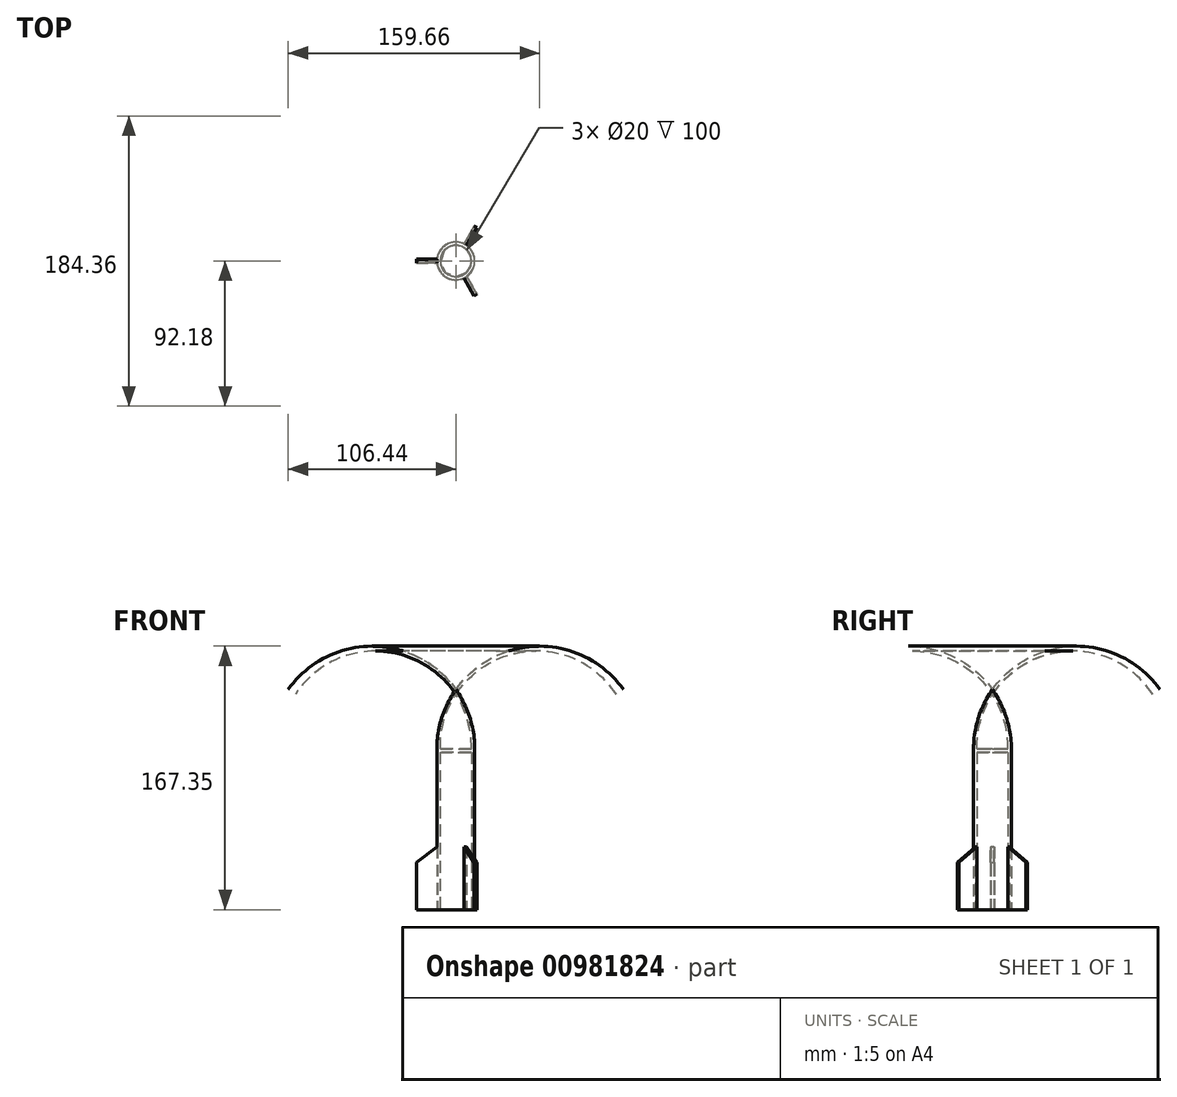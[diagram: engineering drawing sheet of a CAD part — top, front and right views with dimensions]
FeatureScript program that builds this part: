
annotation { "Feature Type Name" : "Feature", "Feature Type Description" : "" }
export const myFeature = defineFeature(function(context is Context, id is Id, definition is map)
    precondition{}
    {
        {
            var Q0;
            Q0=qCreatedBy(makeId("Front.planeOp"),FACE);
            var sketch = newSketch(context, id + "F0", { "sketchPlane" : qUnion([Q0])});
            skLineSegment(sketch, "E0", {"start": v(0, 0) * mm, "end": v(0, 102) * mm});
            skLineSegment(sketch, "E1", {"start": v(-12, 102.13) * mm, "end": v(-12, 0) * mm});
            skLineSegment(sketch, "E2", {"start": v(-12, 0) * mm, "end": v(-10, 0) * mm});
            skLineSegment(sketch, "E3", {"start": v(-10, 0) * mm, "end": v(-10, 100) * mm});
            skLineSegment(sketch, "E4", {"start": v(-10, 100) * mm, "end": v(0, 100) * mm});
            skLineSegment(sketch, "E5", {"start": v(0, 102) * mm, "end": v(-9.84, 102) * mm});
            skLineSegment(sketch, "E6", {"start": v(0, 102) * mm, "end": v(0, 145.97) * mm, "construction": true});
            skArc(sketch, "E7", {"start": v(0, 139.83) * mm, "mid": v(-8.93, 121.9) * mm, "end": v(-12, 102.13) * mm});
            skArc(sketch, "E8", {"start": v(0, 136.66) * mm, "mid": v(-7.55, 120.07) * mm, "end": v(-9.84, 102) * mm});
            skLineSegment(sketch, "E9", {"start": v(0, 139.83) * mm, "end": v(0, 136.66) * mm});
            skSolve(sketch);
        }
        {
            var Q0;
            Q0=qSketchRegion(id+"F0",true);
            var Q1;
            Q1=sQuery(id+"F0.wireOp",EDGE,"E0");
            revolve(context, id + "F1", {"surfaceOperationType" : NewSurfaceOperationType.NEW, "entities" : qUnion([Q0]), "axis" : qUnion([Q1]), "revolveType" : RevolveType.FULL});
        }
        {
            var Q0;
            Q0=qCreatedBy(makeId("Front.planeOp"),FACE);
            var sketch = newSketch(context, id + "F2", { "sketchPlane" : qUnion([Q0])});
            skLineSegment(sketch, "E10", {"start": v(-25, 30) * mm, "end": v(-12, 40) * mm});
            skLineSegment(sketch, "E11", {"start": v(-12, 0) * mm, "end": v(-25, 0) * mm});
            skLineSegment(sketch, "E12", {"start": v(-25, 30) * mm, "end": v(-25, 0) * mm});
            skLineSegment(sketch, "E13.0", {"start": v(12, 0) * mm, "end": v(-12, 0) * mm, "construction": true});
            skLineSegment(sketch, "E14", {"start": v(-12, 0) * mm, "end": v(-12, 102.13) * mm});
            skLineSegment(sketch, "E15", {"start": v(-12, 0) * mm, "end": v(-12, 102.13) * mm, "construction": true});
            skLineSegment(sketch, "E16.bottom", {"start": v(-12, 40) * mm, "end": v(-11.5, 40) * mm});
            skLineSegment(sketch, "E16.top", {"start": v(-12, 0) * mm, "end": v(-11.5, 0) * mm});
            skLineSegment(sketch, "E16.right", {"start": v(-11.5, 40) * mm, "end": v(-11.5, 0) * mm});
            skSolve(sketch);
        }
        {
            var Q0;
            Q0=qSketchRegion(id+"F2",true);
            extrude(context, id + "F3", {"entities" : qUnion([Q0]), "operationType" : NewBodyOperationType.ADD, "endBound" : BoundingType.SYMMETRIC, "depth" : 2 * mm, "offsetDistance" : 25 * mm});
        }
        {
            var Q0;
            Q0=makeQuery(id+"F3.opExtrude","SWEPT_BODY",BODY,{"disambiguationData":[OSD([sQuery(id+"F2.wireOp",EDGE,"e22eb37e-d8dd-4329-a2d3-fbfdff4c98e4"),sQuery(id+"F2.wireOp",EDGE,"lLMWoRsq-RIhi-c7c5-fCH5-DzFpHTFsqkWn"),sQuery(id+"F2.wireOp",EDGE,"E10"),sQuery(id+"F2.wireOp",EDGE,"s4oJCqMo-VKWq-kCVp-h3GD-7KcSVkuLEeKC")])]});
            var Q1;
            Q1=makeQuery(id+"F1.opRevolve","SWEPT_BODY",BODY,{"disambiguationData":[OSD([sQuery(id+"F0.wireOp",EDGE,"E0"),sQuery(id+"F0.wireOp",EDGE,"tzREqpSo-uzh5-If2K-zJL4-kQ3OELhC54iP"),sQuery(id+"F0.wireOp",EDGE,"E1"),sQuery(id+"F0.wireOp",EDGE,"E2"),sQuery(id+"F0.wireOp",EDGE,"E3"),sQuery(id+"F0.wireOp",EDGE,"E4")])]});
            var Q2;
            Q2=makeQuery(id+"F1.opRevolve","SWEPT_FACE",FACE,{"disambiguationData":[OSD([sQuery(id+"F0.wireOp",EDGE,"E1")])]});
            circularPattern(context, id + "F4", {"entities" : qUnion([Q0, Q1]), "axis" : qUnion([Q2]), "angle" : 360 * degree, "instanceCount" : 3, "equalSpace" : true});
        }
        {
            var Q0;
            Q0=qSketchRegion(id+"F2",true);
            extrude(context, id + "F5", {"entities" : qUnion([Q0]), "endBound" : BoundingType.SYMMETRIC, "depth" : 2.5 * mm, "offsetDistance" : 25 * mm});
        }
    });
